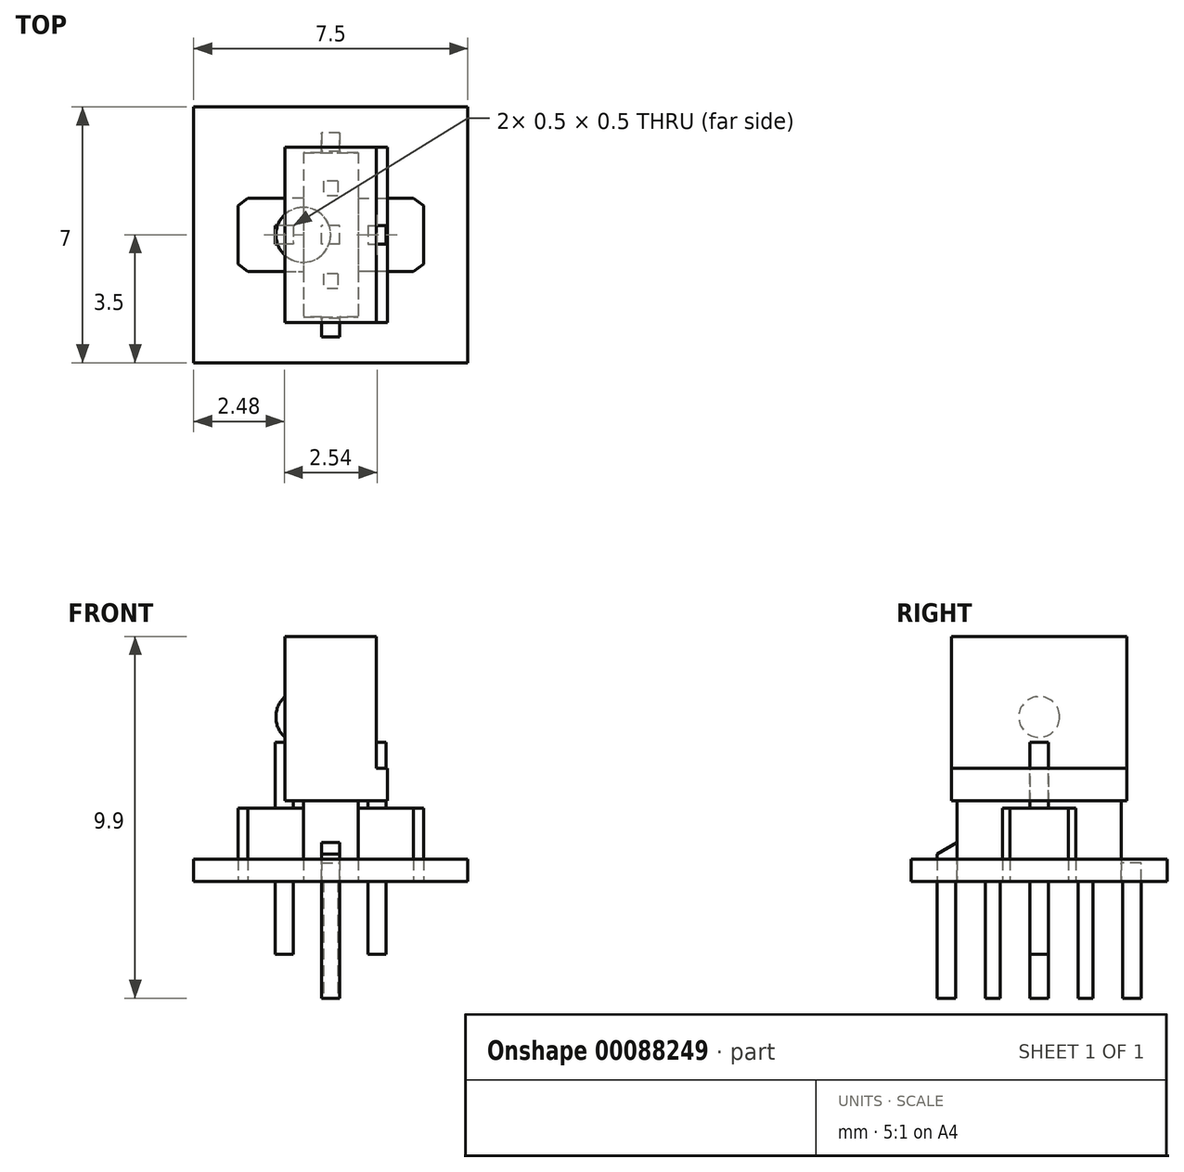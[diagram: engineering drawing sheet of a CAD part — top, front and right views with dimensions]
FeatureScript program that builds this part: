
annotation { "Feature Type Name" : "Feature", "Feature Type Description" : "" }
export const myFeature = defineFeature(function(context is Context, id is Id, definition is map)
    precondition{}
    {
        {
            var Q0;
            Q0=qCreatedBy(makeId("Top.planeOp"),FACE);
            cPlane(context, id + "F0", {"entities" : qUnion([Q0]), "cplaneType" : CPlaneType.OFFSET, "offset" : 2 * mm, "width" : 150 * mm, "height" : 150 * mm});
        }
        {
            var Q0;
            Q0=qCreatedBy(makeId("Front.planeOp"),FACE);
            var sketch = newSketch(context, id + "F1", { "sketchPlane" : qUnion([Q0])});
            skLineSegment(sketch, "E0", {"start": v(-1.25, 6.7) * mm, "end": v(1.25, 6.7) * mm});
            skLineSegment(sketch, "E1", {"start": v(1.25, 6.7) * mm, "end": v(1.25, 3.1) * mm});
            skLineSegment(sketch, "E2", {"start": v(1.25, 3.1) * mm, "end": v(1.55, 3.1) * mm});
            skLineSegment(sketch, "E3", {"start": v(1.55, 3.1) * mm, "end": v(1.55, 2.2) * mm});
            skLineSegment(sketch, "E4", {"start": v(1.55, 2.2) * mm, "end": v(-1.25, 2.2) * mm});
            skLineSegment(sketch, "E5", {"start": v(-1.25, 2.2) * mm, "end": v(-1.25, 6.7) * mm});
            skLineSegment(sketch, "E6", {"start": v(0, 8.99) * mm, "end": v(0, -1.06) * mm, "construction": true});
            skSolve(sketch);
        }
        {
            var Q0;
            Q0=qSketchRegion(id+"F1",true);
            extrude(context, id + "F2", {"entities" : qUnion([Q0]), "depth" : 4.8 * mm, "symmetric" : true});
        }
        {
            var Q0;
            Q0=qCreatedBy(makeId("Right.planeOp"),FACE);
            var sketch = newSketch(context, id + "F3", { "sketchPlane" : qUnion([Q0])});
            skLineSegment(sketch, "E7", {"start": v(0, 9.64) * mm, "end": v(0, -7.18) * mm, "construction": true});
            skLineSegment(sketch, "E8", {"start": v(2.54, 9.53) * mm, "end": v(2.54, -7.04) * mm, "construction": true});
            skLineSegment(sketch, "E9", {"start": v(-2.54, 9.6) * mm, "end": v(-2.54, -6.7) * mm, "construction": true});
            skLineSegment(sketch, "E10.bottom", {"start": v(0.25, 2.2) * mm, "end": v(-0.25, 2.2) * mm});
            skLineSegment(sketch, "E10.top", {"start": v(0.25, -3.2) * mm, "end": v(-0.25, -3.2) * mm});
            skLineSegment(sketch, "E10.left", {"start": v(0.25, 2.2) * mm, "end": v(0.25, -3.2) * mm});
            skLineSegment(sketch, "E10.right", {"start": v(-0.25, 2.2) * mm, "end": v(-0.25, -3.2) * mm});
            skLineSegment(sketch, "E11", {"start": v(1.25, 2.2) * mm, "end": v(1.25, 0) * mm});
            skLineSegment(sketch, "E12", {"start": v(1.25, 0) * mm, "end": v(2.3, 0) * mm});
            skLineSegment(sketch, "E13", {"start": v(2.3, 0) * mm, "end": v(2.3, -3.2) * mm});
            skLineSegment(sketch, "E14", {"start": v(2.3, -3.2) * mm, "end": v(2.8, -3.2) * mm});
            skLineSegment(sketch, "E15", {"start": v(2.8, -3.2) * mm, "end": v(2.8, 0.5) * mm});
            skLineSegment(sketch, "E16", {"start": v(2.8, 0.5) * mm, "end": v(1.75, 0.5) * mm});
            skLineSegment(sketch, "E17", {"start": v(1.75, 0.5) * mm, "end": v(1.75, 2.2) * mm});
            skLineSegment(sketch, "E18", {"start": v(1.75, 2.2) * mm, "end": v(1.25, 2.2) * mm});
            skLineSegment(sketch, "E19", {"start": v(-1.75, 2.2) * mm, "end": v(-1.75, 1.35) * mm});
            skLineSegment(sketch, "E20", {"start": v(-1.75, 1.35) * mm, "end": v(-2.8, 0.75) * mm});
            skLineSegment(sketch, "E21", {"start": v(-2.8, 0.75) * mm, "end": v(-2.8, -3.2) * mm});
            skLineSegment(sketch, "E22", {"start": v(-2.8, -3.2) * mm, "end": v(-2.3, -3.2) * mm});
            skLineSegment(sketch, "E23", {"start": v(-2.29, -3.2) * mm, "end": v(-2.3, 0) * mm});
            skLineSegment(sketch, "E24", {"start": v(-2.3, 0) * mm, "end": v(-1.25, 0) * mm});
            skLineSegment(sketch, "E25", {"start": v(-1.25, 0) * mm, "end": v(-1.25, 2.2) * mm});
            skLineSegment(sketch, "E26", {"start": v(-1.25, 2.2) * mm, "end": v(-1.75, 2.2) * mm});
            skLineSegment(sketch, "E27", {"start": v(4.1, 2.2) * mm, "end": v(-3.46, 2.2) * mm, "construction": true});
            skLineSegment(sketch, "E28", {"start": v(4.32, 0) * mm, "end": v(-4.48, 0) * mm, "construction": true});
            skLineSegment(sketch, "E29", {"start": v(4.16, -3.2) * mm, "end": v(-3.84, -3.2) * mm, "construction": true});
            skSolve(sketch);
        }
        {
            var Q0;
            Q0=qSketchRegion(id+"F3",true);
            extrude(context, id + "F4", {"entities" : qUnion([Q0]), "operationType" : NewBodyOperationType.ADD, "depth" : 0.5 * mm, "symmetric" : true});
        }
        {
            var Q0;
            Q0=qCreatedBy(makeId("Right.planeOp"),FACE);
            var sketch = newSketch(context, id + "F5", { "sketchPlane" : qUnion([Q0])});
            skLineSegment(sketch, "E30.bottom", {"start": v(2.25, 5.7) * mm, "end": v(-2.25, 5.7) * mm});
            skLineSegment(sketch, "E30.top", {"start": v(2.25, 0) * mm, "end": v(-2.25, 0) * mm});
            skLineSegment(sketch, "E30.left", {"start": v(2.25, 5.7) * mm, "end": v(2.25, 0) * mm});
            skLineSegment(sketch, "E30.right", {"start": v(-2.25, 5.7) * mm, "end": v(-2.25, 0) * mm});
            skLineSegment(sketch, "E31", {"start": v(0, 4.8) * mm, "end": v(0, -0.83) * mm, "construction": true});
            skSolve(sketch);
        }
        {
            var Q0;
            Q0=qSketchRegion(id+"F5",true);
            extrude(context, id + "F6", {"entities" : qUnion([Q0]), "depth" : 1.5 * mm, "symmetric" : true});
        }
        {
            var Q0;
            Q0=makeQuery(id+"F6.opExtrude","CAP_FACE",FACE,{"disambiguationData":[OSD([sQuery(id+"F5.wireOp",EDGE,"E30.bottom"),sQuery(id+"F5.wireOp",EDGE,"E30.top"),sQuery(id+"F5.wireOp",EDGE,"E30.left"),sQuery(id+"F5.wireOp",EDGE,"E30.right")])],"isStart":true});
            var sketch = newSketch(context, id + "F7", { "sketchPlane" : qUnion([Q0])});
            skArc(sketch, "E32", {"start": v(0, 5.25) * mm, "mid": v(-0.75, 4.5) * mm, "end": v(0, 3.75) * mm});
            skLineSegment(sketch, "E33", {"start": v(0, 5.25) * mm, "end": v(0, 3.75) * mm});
            skSolve(sketch);
        }
        {
            var Q0;
            Q0=qSketchRegion(id+"F7",true);
            var Q1;
            Q1=sQuery(id+"F7.wireOp",EDGE,"E33");
            revolve(context, id + "F8", {"operationType" : NewBodyOperationType.ADD, "entities" : qUnion([Q0]), "axis" : qUnion([Q1]), "revolveType" : RevolveType.FULL});
        }
        {
            var Q0;
            Q0=qCreatedBy(makeId("Right.planeOp"),FACE);
            var sketch = newSketch(context, id + "F9", { "sketchPlane" : qUnion([Q0])});
            skLineSegment(sketch, "E34", {"start": v(0, 7.5) * mm, "end": v(0, -5.02) * mm, "construction": true});
            skLineSegment(sketch, "E35", {"start": v(4.48, 0) * mm, "end": v(-4.1, 0) * mm, "construction": true});
            skLineSegment(sketch, "E36", {"start": v(-1.27, -3.2) * mm, "end": v(-1.27, 2.43) * mm, "construction": true});
            skLineSegment(sketch, "E37", {"start": v(1.27, 2.43) * mm, "end": v(1.27, -5.32) * mm, "construction": true});
            skLineSegment(sketch, "E38.bottom", {"start": v(1.47, 0) * mm, "end": v(1.07, 0) * mm});
            skLineSegment(sketch, "E38.top", {"start": v(1.47, -3.2) * mm, "end": v(1.07, -3.2) * mm});
            skLineSegment(sketch, "E38.left", {"start": v(1.47, 0) * mm, "end": v(1.47, -3.2) * mm});
            skLineSegment(sketch, "E38.right", {"start": v(1.07, 0) * mm, "end": v(1.07, -3.2) * mm});
            skLineSegment(sketch, "E39.bottom", {"start": v(-1.07, 0) * mm, "end": v(-1.47, 0) * mm});
            skLineSegment(sketch, "E39.top", {"start": v(-1.07, -3.2) * mm, "end": v(-1.47, -3.2) * mm});
            skLineSegment(sketch, "E39.left", {"start": v(-1.07, 0) * mm, "end": v(-1.07, -3.2) * mm});
            skLineSegment(sketch, "E39.right", {"start": v(-1.47, 0) * mm, "end": v(-1.47, -3.2) * mm});
            skSolve(sketch);
        }
        {
            var Q0;
            Q0=qSketchRegion(id+"F9",true);
            extrude(context, id + "F10", {"entities" : qUnion([Q0]), "operationType" : NewBodyOperationType.ADD, "depth" : 0.4 * mm, "symmetric" : true});
        }
        {
            var Q0;
            Q0=qCreatedBy(makeId("Top.planeOp"),FACE);
            var sketch = newSketch(context, id + "F11", { "sketchPlane" : qUnion([Q0])});
            skLineSegment(sketch, "E40", {"start": v(0, 0.8) * mm, "end": v(0.27, 1) * mm});
            skLineSegment(sketch, "E41", {"start": v(0.27, 1) * mm, "end": v(2.27, 1) * mm});
            skLineSegment(sketch, "E42", {"start": v(2.27, 1) * mm, "end": v(2.54, 0.8) * mm});
            skLineSegment(sketch, "E43", {"start": v(2.54, 0.8) * mm, "end": v(2.54, -0.8) * mm});
            skLineSegment(sketch, "E44", {"start": v(2.54, -0.8) * mm, "end": v(2.27, -1) * mm});
            skLineSegment(sketch, "E45", {"start": v(2.27, -1) * mm, "end": v(0.27, -1) * mm});
            skLineSegment(sketch, "E46", {"start": v(0.27, -1) * mm, "end": v(0, -0.8) * mm});
            skLineSegment(sketch, "E47", {"start": v(0, -0.8) * mm, "end": v(0, 0.8) * mm});
            skLineSegment(sketch, "E48", {"start": v(0, 2.31) * mm, "end": v(0, -1.41) * mm, "construction": true});
            skLineSegment(sketch, "E49", {"start": v(-0.3, 0) * mm, "end": v(0.1, 0) * mm, "construction": true});
            skLineSegment(sketch, "E50", {"start": v(1.27, 0.8) * mm, "end": v(1.27, -1.33) * mm, "construction": true});
            skLineSegment(sketch, "E51.bottom", {"start": v(1.02, 0.25) * mm, "end": v(1.52, 0.25) * mm});
            skLineSegment(sketch, "E51.top", {"start": v(1.02, -0.25) * mm, "end": v(1.52, -0.25) * mm});
            skLineSegment(sketch, "E51.left", {"start": v(1.02, 0.25) * mm, "end": v(1.02, -0.25) * mm});
            skLineSegment(sketch, "E51.right", {"start": v(1.52, 0.25) * mm, "end": v(1.52, -0.25) * mm});
            skLineSegment(sketch, "E52.0.MirrorCS", {"start": v(-0.27, 1) * mm, "end": v(-2.27, 1) * mm});
            skLineSegment(sketch, "E52.1.MirrorCS", {"start": v(-2.27, 1) * mm, "end": v(-2.54, 0.8) * mm});
            skLineSegment(sketch, "E52.2.MirrorCS", {"start": v(0, 0.8) * mm, "end": v(-0.27, 1) * mm});
            skLineSegment(sketch, "E52.3.MirrorCS", {"start": v(-1.02, 0.25) * mm, "end": v(-1.52, 0.25) * mm});
            skLineSegment(sketch, "E52.4.MirrorCS", {"start": v(-1.52, 0.25) * mm, "end": v(-1.52, -0.25) * mm});
            skLineSegment(sketch, "E52.5.MirrorCS", {"start": v(-1.02, 0.25) * mm, "end": v(-1.02, -0.25) * mm});
            skLineSegment(sketch, "E52.6.MirrorCS", {"start": v(-1.02, -0.25) * mm, "end": v(-1.52, -0.25) * mm});
            skLineSegment(sketch, "E52.7.MirrorCS", {"start": v(-2.54, 0.8) * mm, "end": v(-2.54, -0.8) * mm});
            skLineSegment(sketch, "E52.9.MirrorCS", {"start": v(-2.54, -0.8) * mm, "end": v(-2.27, -1) * mm});
            skLineSegment(sketch, "E52.10.MirrorCS", {"start": v(-2.27, -1) * mm, "end": v(-0.27, -1) * mm});
            skLineSegment(sketch, "E52.11.MirrorCS", {"start": v(-0.27, -1) * mm, "end": v(0, -0.8) * mm});
            skSolve(sketch);
        }
        {
            var Q0;
            Q0=qSketchRegion(id+"F11",true);
            extrude(context, id + "F12", {"entities" : qUnion([Q0]), "depth" : 2 * mm});
        }
        {
            var Q0;
            Q0=makeQuery(id+"F12.opExtrude","CAP_FACE",FACE,{"disambiguationData":[OSD([sQuery(id+"F11.wireOp",EDGE,"E40"),sQuery(id+"F11.wireOp",EDGE,"E41"),sQuery(id+"F11.wireOp",EDGE,"E42"),sQuery(id+"F11.wireOp",EDGE,"E43"),sQuery(id+"F11.wireOp",EDGE,"E44"),sQuery(id+"F11.wireOp",EDGE,"E45"),sQuery(id+"F11.wireOp",EDGE,"E46"),sQuery(id+"F11.wireOp",EDGE,"E51.bottom"),sQuery(id+"F11.wireOp",EDGE,"E51.top"),sQuery(id+"F11.wireOp",EDGE,"E51.left"),sQuery(id+"F11.wireOp",EDGE,"E51.right"),sQuery(id+"F11.wireOp",EDGE,"E52.0.MirrorCS"),sQuery(id+"F11.wireOp",EDGE,"E52.1.MirrorCS"),sQuery(id+"F11.wireOp",EDGE,"E52.2.MirrorCS"),sQuery(id+"F11.wireOp",EDGE,"E52.3.MirrorCS"),sQuery(id+"F11.wireOp",EDGE,"E52.4.MirrorCS"),sQuery(id+"F11.wireOp",EDGE,"E52.5.MirrorCS"),sQuery(id+"F11.wireOp",EDGE,"E52.6.MirrorCS"),sQuery(id+"F11.wireOp",EDGE,"E52.7.MirrorCS"),sQuery(id+"F11.wireOp",EDGE,"E52.9.MirrorCS"),sQuery(id+"F11.wireOp",EDGE,"E52.10.MirrorCS"),sQuery(id+"F11.wireOp",EDGE,"E52.11.MirrorCS")])],"isStart":false});
            var sketch = newSketch(context, id + "F13", { "sketchPlane" : qUnion([Q0])});
            skLineSegment(sketch, "E53.0", {"start": v(1.02, 0.25) * mm, "end": v(1.52, 0.25) * mm});
            skLineSegment(sketch, "E53.1", {"start": v(1.52, 0.25) * mm, "end": v(1.52, -0.25) * mm});
            skLineSegment(sketch, "E53.2", {"start": v(1.02, -0.25) * mm, "end": v(1.52, -0.25) * mm});
            skLineSegment(sketch, "E53.3", {"start": v(1.02, 0.25) * mm, "end": v(1.02, -0.25) * mm});
            skLineSegment(sketch, "E54.0", {"start": v(-1.02, 0.25) * mm, "end": v(-1.52, 0.25) * mm});
            skLineSegment(sketch, "E54.1", {"start": v(-1.02, 0.25) * mm, "end": v(-1.02, -0.25) * mm});
            skLineSegment(sketch, "E54.3", {"start": v(-1.52, 0.25) * mm, "end": v(-1.52, -0.25) * mm});
            skLineSegment(sketch, "E54.4", {"start": v(-1.02, -0.25) * mm, "end": v(-1.52, -0.25) * mm});
            skSolve(sketch);
        }
        {
            var Q0;
            Q0=qSketchRegion(id+"F13",true);
            extrude(context, id + "F14", {"entities" : qUnion([Q0]), "operationType" : NewBodyOperationType.ADD, "depth" : 1.8 * mm, "hasSecondDirection" : true, "secondDirectionOppositeDirection" : true, "secondDirectionDepth" : 4 * mm});
        }
        {
            var Q0;
            Q0=qCreatedBy(makeId("Top.planeOp"),FACE);
            var sketch = newSketch(context, id + "F15", { "sketchPlane" : qUnion([Q0])});
            skLineSegment(sketch, "E55.bottom", {"start": v(3.75, 3.5) * mm, "end": v(-3.75, 3.5) * mm});
            skLineSegment(sketch, "E55.top", {"start": v(3.75, -3.5) * mm, "end": v(-3.75, -3.5) * mm});
            skLineSegment(sketch, "E55.left", {"start": v(3.75, 3.5) * mm, "end": v(3.75, -3.5) * mm});
            skLineSegment(sketch, "E55.right", {"start": v(-3.75, 3.5) * mm, "end": v(-3.75, -3.5) * mm});
            skPoint(sketch, "E55.middle", {"position": v(0, 0) * mm});
            skSolve(sketch);
        }
        {
            var Q0;
            Q0=qSketchRegion(id+"F15",true);
            extrude(context, id + "F16", {"entities" : qUnion([Q0]), "depth" : 0.6 * mm});
        }
    });
